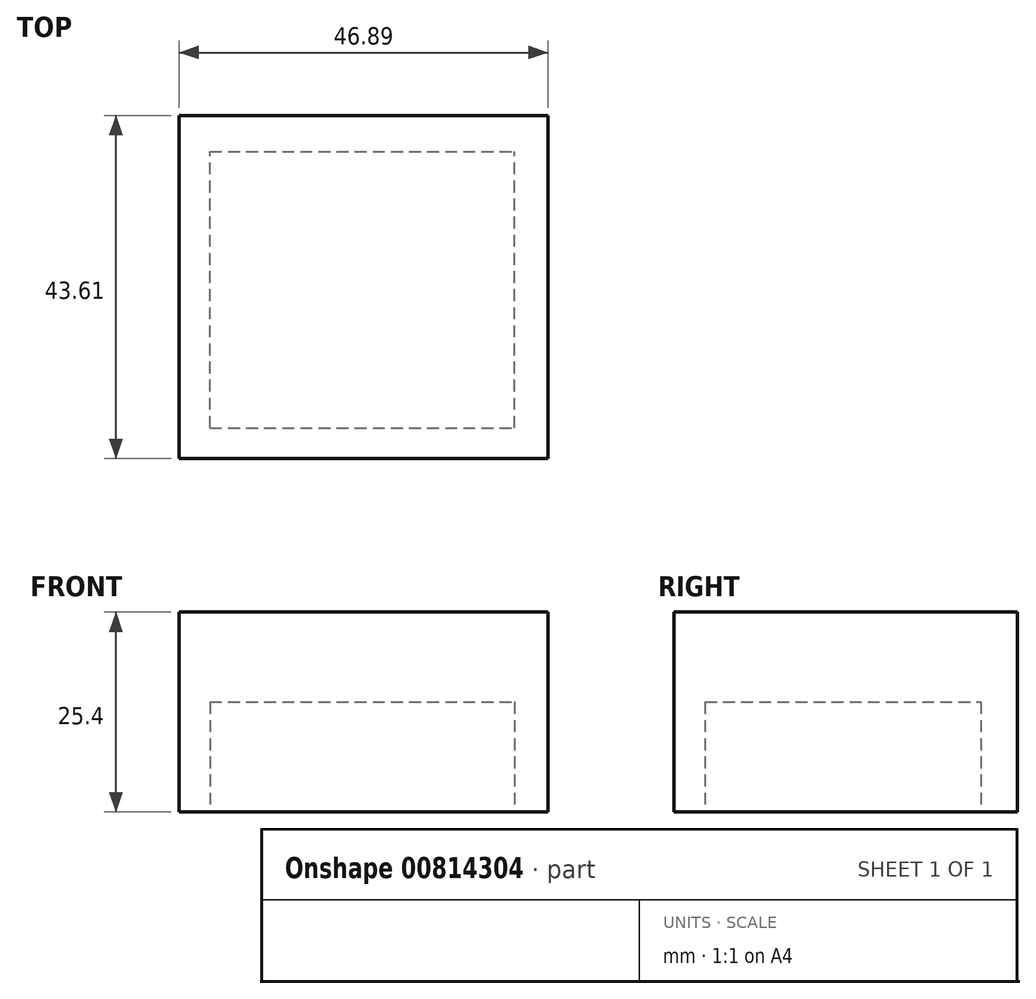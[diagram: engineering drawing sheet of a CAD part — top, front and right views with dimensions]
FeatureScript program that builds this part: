
annotation { "Feature Type Name" : "Feature", "Feature Type Description" : "" }
export const myFeature = defineFeature(function(context is Context, id is Id, definition is map)
    precondition{}
    {
        {
            var Q0;
            Q0=qCreatedBy(makeId("Top.planeOp"),FACE);
            var sketch = newSketch(context, id + "F0", { "sketchPlane" : qUnion([Q0])});
            skLineSegment(sketch, "E0.bottom", {"start": v(1.15, 17.32) * mm, "end": v(48.04, 17.32) * mm});
            skLineSegment(sketch, "E0.top", {"start": v(1.15, -26.3) * mm, "end": v(48.04, -26.3) * mm});
            skLineSegment(sketch, "E0.left", {"start": v(1.15, 17.32) * mm, "end": v(1.15, -26.3) * mm});
            skLineSegment(sketch, "E0.right", {"start": v(48.04, 17.32) * mm, "end": v(48.04, -26.3) * mm});
            skSolve(sketch);
        }
        {
            var Q0;
            Q0 = qSketchRegion(id + "F0", true);
            extrude(context, id + "F1", {"entities" : qUnion([Q0]), "depth" : 25.4 * mm, "offsetDistance" : 25.4 * mm});
        }
        {
            var Q0;
            Q0=makeQuery(id+"F1.opExtrude","CAP_FACE",FACE,{"disambiguationData":[OSD([sQuery(id+"F0.wireOp",EDGE,"E0.bottom"),sQuery(id+"F0.wireOp",EDGE,"E0.top"),sQuery(id+"F0.wireOp",EDGE,"E0.left"),sQuery(id+"F0.wireOp",EDGE,"E0.right")])],"isStart":true});
            var sketch = newSketch(context, id + "F2", { "sketchPlane" : qUnion([Q0])});
            skLineSegment(sketch, "E1.bottom", {"start": v(5.09, 22.36) * mm, "end": v(43.77, 22.36) * mm});
            skLineSegment(sketch, "E1.top", {"start": v(5.09, -12.72) * mm, "end": v(43.77, -12.72) * mm});
            skLineSegment(sketch, "E1.left", {"start": v(5.09, 22.36) * mm, "end": v(5.09, -12.72) * mm});
            skLineSegment(sketch, "E1.right", {"start": v(43.77, 22.36) * mm, "end": v(43.77, -12.72) * mm});
            skSolve(sketch);
        }
        {
            var Q0;
            Q0 = qSketchRegion(id + "F2", true);
            extrude(context, id + "F3", {"entities" : qUnion([Q0]), "operationType" : NewBodyOperationType.REMOVE, "oppositeDirection" : true, "depth" : 13.97 * mm, "offsetDistance" : 25.4 * mm});
        }
    });
